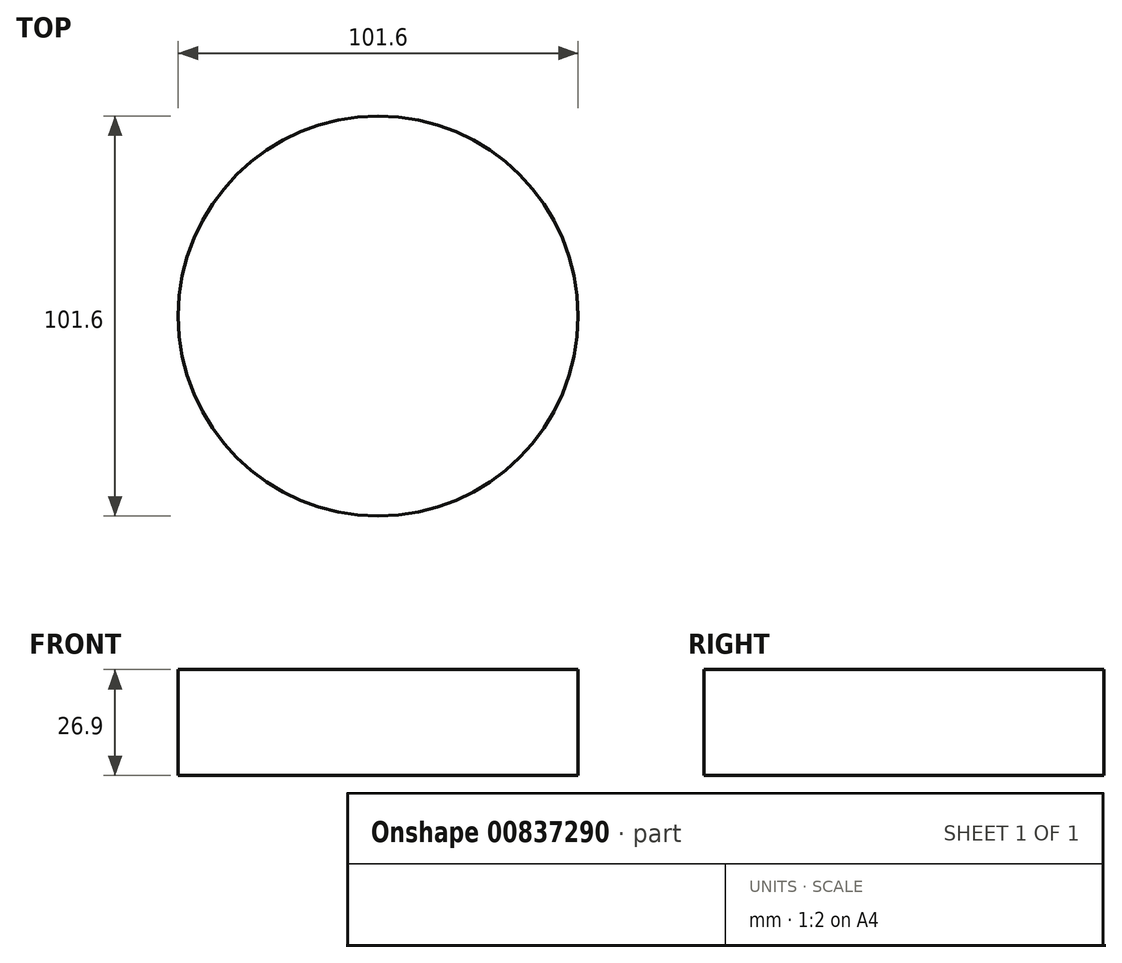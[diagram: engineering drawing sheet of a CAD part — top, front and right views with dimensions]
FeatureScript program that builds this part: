
annotation { "Feature Type Name" : "Feature", "Feature Type Description" : "" }
export const myFeature = defineFeature(function(context is Context, id is Id, definition is map)
    precondition{}
    {
        {
            var Q0;
            Q0=qCreatedBy(makeId("Top.planeOp"),FACE);
            var sketch = newSketch(context, id + "F0", { "sketchPlane" : qUnion([Q0])});
            skCircle(sketch, "E0", {"center": v(0, 0) * mm, "radius": 50.8 * mm});
            skSolve(sketch);
        }
        {
            var Q0;
            Q0=makeQuery(id+"F0.imprint","IMPRINT",FACE,{"disambiguationData":[TD([[makeQuery(id+"F0.imprint","IMPRINT",EDGE,{"derivedFrom":sQuery(id+"F0.wireOp",EDGE,"E0")}),1.0]])]});
            extrude(context, id + "F1", {"entities" : qUnion([Q0]), "depth" : 1.5 * mm, "offsetDistance" : 25.4 * mm});
        }
        {
            var Q0;
            Q0=makeQuery(id+"F1.opExtrude","CAP_FACE",FACE,{"disambiguationData":[OSD([sQuery(id+"F0.wireOp",EDGE,"E0")])],"isStart":false});
            var sketch = newSketch(context, id + "F2", { "sketchPlane" : qUnion([Q0])});
            skCircle(sketch, "E1", {"center": v(0, 0) * mm, "radius": 1.5 * mm});
            skSolve(sketch);
        }
        {
            var Q0;
            Q0 = qSketchRegion(id + "F2", true);
            var Q1;
            Q1=makeQuery(id+"F2.imprint","IMPRINT",FACE,{"disambiguationData":[TD([[makeQuery(id+"F2.imprint","IMPRINT",EDGE,{"derivedFrom":sQuery(id+"F2.wireOp",EDGE,"E1")}),-1.0]])]});
            extrude(context, id + "F3", {"entities" : qUnion([Q0, Q1]), "operationType" : NewBodyOperationType.ADD, "depth" : 25.4 * mm, "offsetDistance" : 25.4 * mm});
        }
    });
